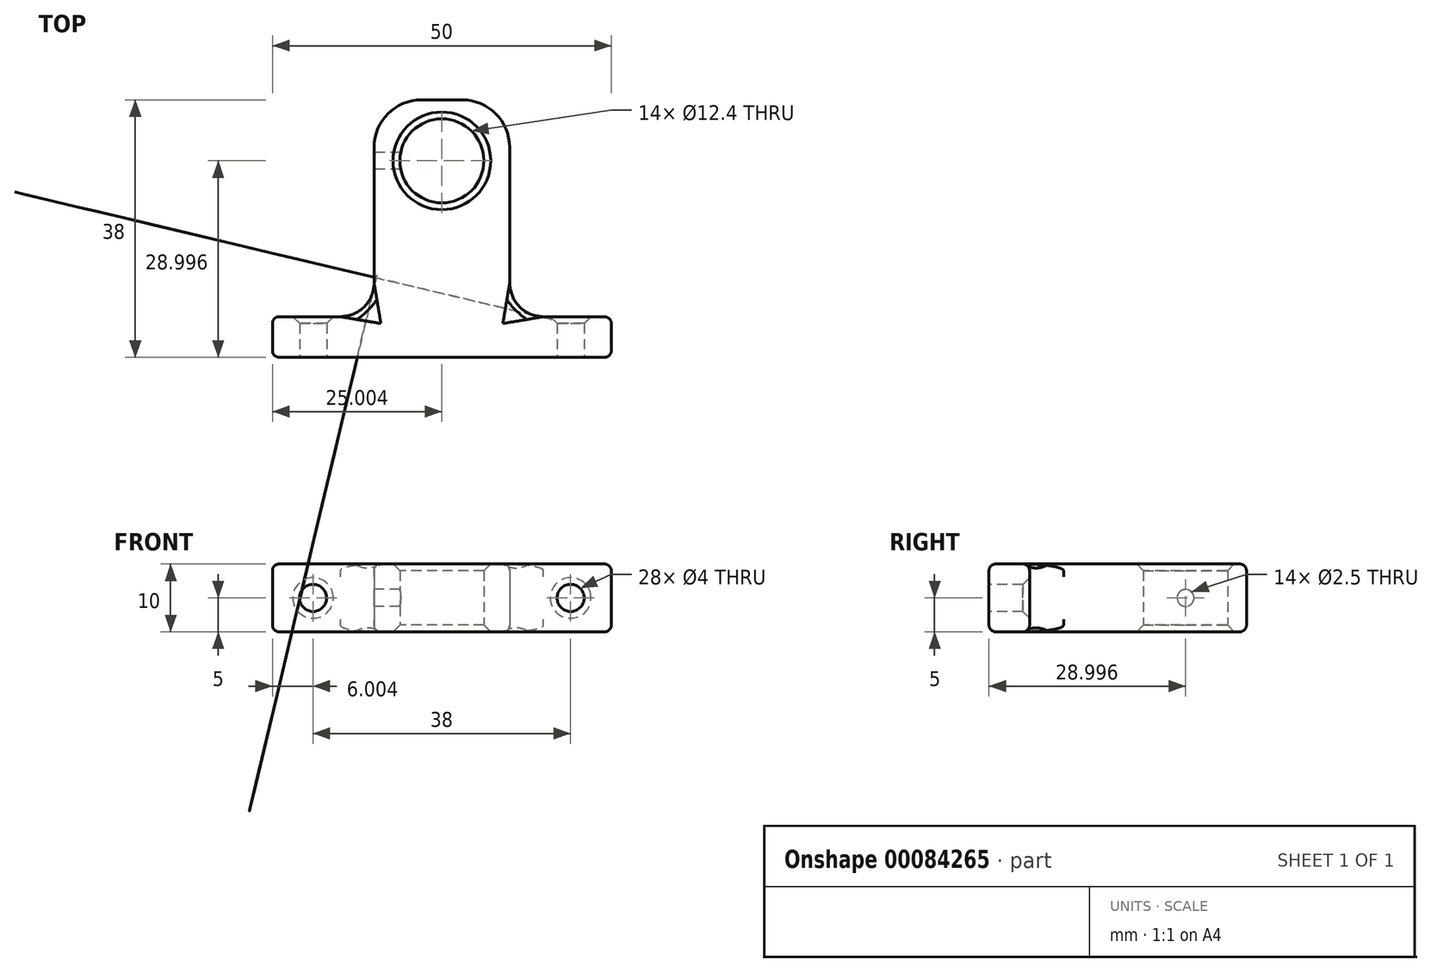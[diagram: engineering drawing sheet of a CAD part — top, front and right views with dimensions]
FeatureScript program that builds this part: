
annotation { "Feature Type Name" : "Feature", "Feature Type Description" : "" }
export const myFeature = defineFeature(function(context is Context, id is Id, definition is map)
    precondition{}
    {
        {
            var Q0;
            Q0=qCreatedBy(makeId("Top.planeOp"),FACE);
            var sketch = newSketch(context, id + "F0", { "sketchPlane" : qUnion([Q0])});
            skLineSegment(sketch, "E0", {"start": v(-22.94, -2.82) * mm, "end": v(27.06, -2.82) * mm});
            skLineSegment(sketch, "E1", {"start": v(27.06, -2.82) * mm, "end": v(27.06, 3.18) * mm});
            skLineSegment(sketch, "E2", {"start": v(27.06, 3.18) * mm, "end": v(12.06, 3.18) * mm});
            skLineSegment(sketch, "E3", {"start": v(12.06, 3.18) * mm, "end": v(12.06, 28.18) * mm});
            skLineSegment(sketch, "E4", {"start": v(-7.94, 3.18) * mm, "end": v(-22.94, 3.18) * mm});
            skLineSegment(sketch, "E5", {"start": v(-22.94, 3.18) * mm, "end": v(-22.94, -2.82) * mm});
            skLineSegment(sketch, "E6", {"start": v(-7.94, 28.18) * mm, "end": v(-7.94, 3.18) * mm});
            skLineSegment(sketch, "E7", {"start": v(-0.94, 35.18) * mm, "end": v(5.06, 35.18) * mm});
            skLineSegment(sketch, "E8", {"start": v(2.06, 35.18) * mm, "end": v(2.06, 26.18) * mm});
            skLineSegment(sketch, "E9", {"start": v(2.06, 26.18) * mm, "end": v(2.06, -2.82) * mm});
            skCircle(sketch, "E10", {"center": v(2.06, 26.18) * mm, "radius": 6.2 * mm});
            skPoint(sketch, "E11.visualSharp", {"position": v(-7.94, 35.18) * mm});
            skArc(sketch, "E11.filletArc", {"start": v(-0.94, 35.18) * mm, "mid": v(-5.89, 33.13) * mm, "end": v(-7.94, 28.18) * mm});
            skPoint(sketch, "E12.visualSharp", {"position": v(12.06, 35.18) * mm});
            skArc(sketch, "E12.filletArc", {"start": v(12.06, 28.18) * mm, "mid": v(10.01, 33.13) * mm, "end": v(5.06, 35.18) * mm});
            skSolve(sketch);
        }
        {
            var Q0;
            {var subQ5=sQuery(id+"F0.wireOp",EDGE,"E1");Q0=makeQuery(id+"F0.imprint","IMPRINT",FACE,{"disambiguationData":[TD([[makeQuery(id+"F0.imprint","IMPRINT",EDGE,{"derivedFrom":subQ5}),1.0]])]});}
            var Q1;
            Q1=makeQuery(id+"F0.imprint","IMPRINT",FACE,{"disambiguationData":[TD([[makeQuery(id+"F0.imprint","IMPRINT",EDGE,{"derivedFrom":sQuery(id+"F0.wireOp",EDGE,"E4")}),1.0]])]});
            extrude(context, id + "F1", {"entities" : qUnion([Q0, Q1]), "depth" : 10 * mm});
        }
        {
            var Q0;
            Q0=makeQuery(id+"F1.opExtrude","CAP_EDGE",EDGE,{"disambiguationData":[OSD([sQuery(id+"F0.wireOp",EDGE,"E12.filletArc")])],"isStart":false});
            var Q1;
            Q1=makeQuery(id+"F1.opExtrude","CAP_EDGE",EDGE,{"disambiguationData":[OSD([sQuery(id+"F0.wireOp",EDGE,"E3")])],"isStart":false});
            var Q2;
            Q2=makeQuery(id+"F1.opExtrude","CAP_EDGE",EDGE,{"disambiguationData":[OSD([sQuery(id+"F0.wireOp",EDGE,"E2")])],"isStart":false});
            var Q3;
            Q3=makeQuery(id+"F1.opExtrude","CAP_EDGE",EDGE,{"disambiguationData":[OSD([sQuery(id+"F0.wireOp",EDGE,"E1")])],"isStart":false});
            var Q4;
            Q4=makeQuery(id+"F1.opExtrude","CAP_EDGE",EDGE,{"disambiguationData":[OSD([sQuery(id+"F0.wireOp",EDGE,"E0")])],"isStart":false});
            var Q5;
            Q5=makeQuery(id+"F1.opExtrude","CAP_EDGE",EDGE,{"disambiguationData":[OSD([sQuery(id+"F0.wireOp",EDGE,"E5")])],"isStart":false});
            var Q6;
            Q6=makeQuery(id+"F1.opExtrude","CAP_EDGE",EDGE,{"disambiguationData":[OSD([sQuery(id+"F0.wireOp",EDGE,"E4")])],"isStart":false});
            var Q7;
            Q7=makeQuery(id+"F1.opExtrude","CAP_EDGE",EDGE,{"disambiguationData":[OSD([sQuery(id+"F0.wireOp",EDGE,"E6")])],"isStart":false});
            var Q8;
            Q8=makeQuery(id+"F1.opExtrude","CAP_EDGE",EDGE,{"disambiguationData":[OSD([sQuery(id+"F0.wireOp",EDGE,"E11.filletArc")])],"isStart":false});
            var Q9;
            Q9=makeQuery(id+"F1.opExtrude","CAP_EDGE",EDGE,{"disambiguationData":[OSD([sQuery(id+"F0.wireOp",EDGE,"E7")])],"isStart":false});
            var Q10;
            Q10=makeQuery(id+"F1.opExtrude","CAP_EDGE",EDGE,{"disambiguationData":[OSD([sQuery(id+"F0.wireOp",EDGE,"E0")])],"isStart":true});
            var Q11;
            Q11=makeQuery(id+"F1.opExtrude","CAP_EDGE",EDGE,{"disambiguationData":[OSD([sQuery(id+"F0.wireOp",EDGE,"E1")])],"isStart":true});
            var Q12;
            Q12=makeQuery(id+"F1.opExtrude","CAP_EDGE",EDGE,{"disambiguationData":[OSD([sQuery(id+"F0.wireOp",EDGE,"E2")])],"isStart":true});
            var Q13;
            Q13=makeQuery(id+"F1.opExtrude","CAP_EDGE",EDGE,{"disambiguationData":[OSD([sQuery(id+"F0.wireOp",EDGE,"E3")])],"isStart":true});
            var Q14;
            Q14=makeQuery(id+"F1.opExtrude","CAP_EDGE",EDGE,{"disambiguationData":[OSD([sQuery(id+"F0.wireOp",EDGE,"E12.filletArc")])],"isStart":true});
            var Q15;
            Q15=makeQuery(id+"F1.opExtrude","CAP_EDGE",EDGE,{"disambiguationData":[OSD([sQuery(id+"F0.wireOp",EDGE,"E7")])],"isStart":true});
            var Q16;
            Q16=makeQuery(id+"F1.opExtrude","CAP_EDGE",EDGE,{"disambiguationData":[OSD([sQuery(id+"F0.wireOp",EDGE,"E11.filletArc")])],"isStart":true});
            var Q17;
            Q17=makeQuery(id+"F1.opExtrude","CAP_EDGE",EDGE,{"disambiguationData":[OSD([sQuery(id+"F0.wireOp",EDGE,"E6")])],"isStart":true});
            var Q18;
            Q18=makeQuery(id+"F1.opExtrude","CAP_EDGE",EDGE,{"disambiguationData":[OSD([sQuery(id+"F0.wireOp",EDGE,"E4")])],"isStart":true});
            var Q19;
            Q19=makeQuery(id+"F1.opExtrude","CAP_EDGE",EDGE,{"disambiguationData":[OSD([sQuery(id+"F0.wireOp",EDGE,"E5")])],"isStart":true});
            var Q20;
            Q20=makeQuery(id+"F1.opExtrude","SWEPT_EDGE",EDGE,{"disambiguationData":[OSD([sQuery(id+"F0.wireOp",EDGE,"E4"),sQuery(id+"F0.wireOp",EDGE,"E5")])]});
            var Q21;
            Q21=makeQuery(id+"F1.opExtrude","SWEPT_EDGE",EDGE,{"disambiguationData":[OSD([sQuery(id+"F0.wireOp",EDGE,"E0"),sQuery(id+"F0.wireOp",EDGE,"E5")])]});
            var Q22;
            Q22=makeQuery(id+"F1.opExtrude","SWEPT_EDGE",EDGE,{"disambiguationData":[OSD([sQuery(id+"F0.wireOp",EDGE,"E0"),sQuery(id+"F0.wireOp",EDGE,"E1")])]});
            var Q23;
            Q23=makeQuery(id+"F1.opExtrude","SWEPT_EDGE",EDGE,{"disambiguationData":[OSD([sQuery(id+"F0.wireOp",EDGE,"E1"),sQuery(id+"F0.wireOp",EDGE,"E2")])]});
            fillet(context, id + "F2", {"entities" : qUnion([Q0, Q1, Q2, Q3, Q4, Q5, Q6, Q7, Q8, Q9, Q10, Q11, Q12, Q13, Q14, Q15, Q16, Q17, Q18, Q19, Q20, Q21, Q22, Q23]), "radius" : 1 * mm, "tangentPropagation" : true, "allowEdgeOverflow" : false});
        }
        {
            var Q0;
            Q0=makeQuery(id+"F1.opExtrude","CAP_EDGE",EDGE,{"disambiguationData":[OSD([sQuery(id+"F0.wireOp",EDGE,"E10")])],"isStart":true});
            var Q1;
            Q1=makeQuery(id+"F1.opExtrude","CAP_EDGE",EDGE,{"disambiguationData":[OSD([sQuery(id+"F0.wireOp",EDGE,"E10")])],"isStart":false});
            chamfer(context, id + "F3", {"entities" : qUnion([Q0, Q1]), "width" : 1 * mm, "tangentPropagation" : true});
        }
        {
            var Q0;
            Q0=makeQuery(id+"F1.opExtrude","SWEPT_EDGE",EDGE,{"disambiguationData":[OSD([sQuery(id+"F0.wireOp",EDGE,"E2"),sQuery(id+"F0.wireOp",EDGE,"E3")])]});
            var Q1;
            Q1=makeQuery(id+"F1.opExtrude","SWEPT_EDGE",EDGE,{"disambiguationData":[OSD([sQuery(id+"F0.wireOp",EDGE,"E4"),sQuery(id+"F0.wireOp",EDGE,"E6")])]});
            fillet(context, id + "F4", {"entities" : qUnion([Q0, Q1]), "radius" : 5 * mm, "tangentPropagation" : true, "allowEdgeOverflow" : false});
        }
        {
            var Q0;
            Q0=makeQuery(id+"F1.opExtrude","SWEPT_FACE",FACE,{"disambiguationData":[OSD([sQuery(id+"F0.wireOp",EDGE,"E0")])]});
            var sketch = newSketch(context, id + "F5", { "sketchPlane" : qUnion([Q0])});
            skLineSegment(sketch, "E13", {"start": v(-21.94, 5) * mm, "end": v(-16.94, 5) * mm});
            skLineSegment(sketch, "E14", {"start": v(26.06, 5) * mm, "end": v(21.06, 5) * mm});
            skCircle(sketch, "E15", {"center": v(-16.94, 5) * mm, "radius": 2 * mm});
            skCircle(sketch, "E16", {"center": v(21.06, 5) * mm, "radius": 2 * mm});
            skSolve(sketch);
        }
        {
            var Q0;
            Q0=makeQuery(id+"F5.imprint","IMPRINT",FACE,{"disambiguationData":[TD([[makeQuery(id+"F5.imprint","IMPRINT",EDGE,{"derivedFrom":sQuery(id+"F5.wireOp",EDGE,"E15")}),1.0]])]});
            var Q1;
            Q1=makeQuery(id+"F5.imprint","IMPRINT",FACE,{"disambiguationData":[TD([[makeQuery(id+"F5.imprint","IMPRINT",EDGE,{"derivedFrom":sQuery(id+"F5.wireOp",EDGE,"E16")}),1.0]])]});
            extrude(context, id + "F6", {"entities" : qUnion([Q0, Q1]), "operationType" : NewBodyOperationType.REMOVE, "oppositeDirection" : true, "depth" : 10 * mm});
        }
        {
            var Q0;
            Q0=makeQuery(id+"F6.boolean.opBoolean","INTERSECT",EDGE,{"derivedFrom":[makeQuery(id+"F1.opExtrude","SWEPT_FACE",FACE,{"disambiguationData":[OSD([sQuery(id+"F0.wireOp",EDGE,"E4")])]}),makeQuery(id+"F6.opExtrude","SWEPT_FACE",FACE,{"disambiguationData":[OSD([sQuery(id+"F5.wireOp",EDGE,"E15")])]})]});
            var Q1;
            Q1=makeQuery(id+"F6.boolean.opBoolean","INTERSECT",EDGE,{"derivedFrom":[makeQuery(id+"F1.opExtrude","SWEPT_FACE",FACE,{"disambiguationData":[OSD([sQuery(id+"F0.wireOp",EDGE,"E2")])]}),makeQuery(id+"F6.opExtrude","SWEPT_FACE",FACE,{"disambiguationData":[OSD([sQuery(id+"F5.wireOp",EDGE,"E16")])]})]});
            chamfer(context, id + "F7", {"entities" : qUnion([Q0, Q1]), "width" : 1 * mm, "tangentPropagation" : true});
        }
        {
            var Q0;
            Q0=makeQuery(id+"F1.opExtrude","SWEPT_FACE",FACE,{"disambiguationData":[OSD([sQuery(id+"F0.wireOp",EDGE,"E6")])]});
            var sketch = newSketch(context, id + "F8", { "sketchPlane" : qUnion([Q0])});
            skLineSegment(sketch, "E17", {"start": v(-28.18, 5) * mm, "end": v(-26.18, 5) * mm});
            skCircle(sketch, "E18", {"center": v(-26.18, 5) * mm, "radius": 1.25 * mm});
            skSolve(sketch);
        }
        {
            var Q0;
            Q0=makeQuery(id+"F8.imprint","IMPRINT",FACE,{"disambiguationData":[TD([[makeQuery(id+"F8.imprint","IMPRINT",EDGE,{"derivedFrom":sQuery(id+"F8.wireOp",EDGE,"E18")}),1.0]])]});
            extrude(context, id + "F9", {"entities" : qUnion([Q0]), "operationType" : NewBodyOperationType.REMOVE, "oppositeDirection" : true, "depth" : 6 * mm});
        }
    });
